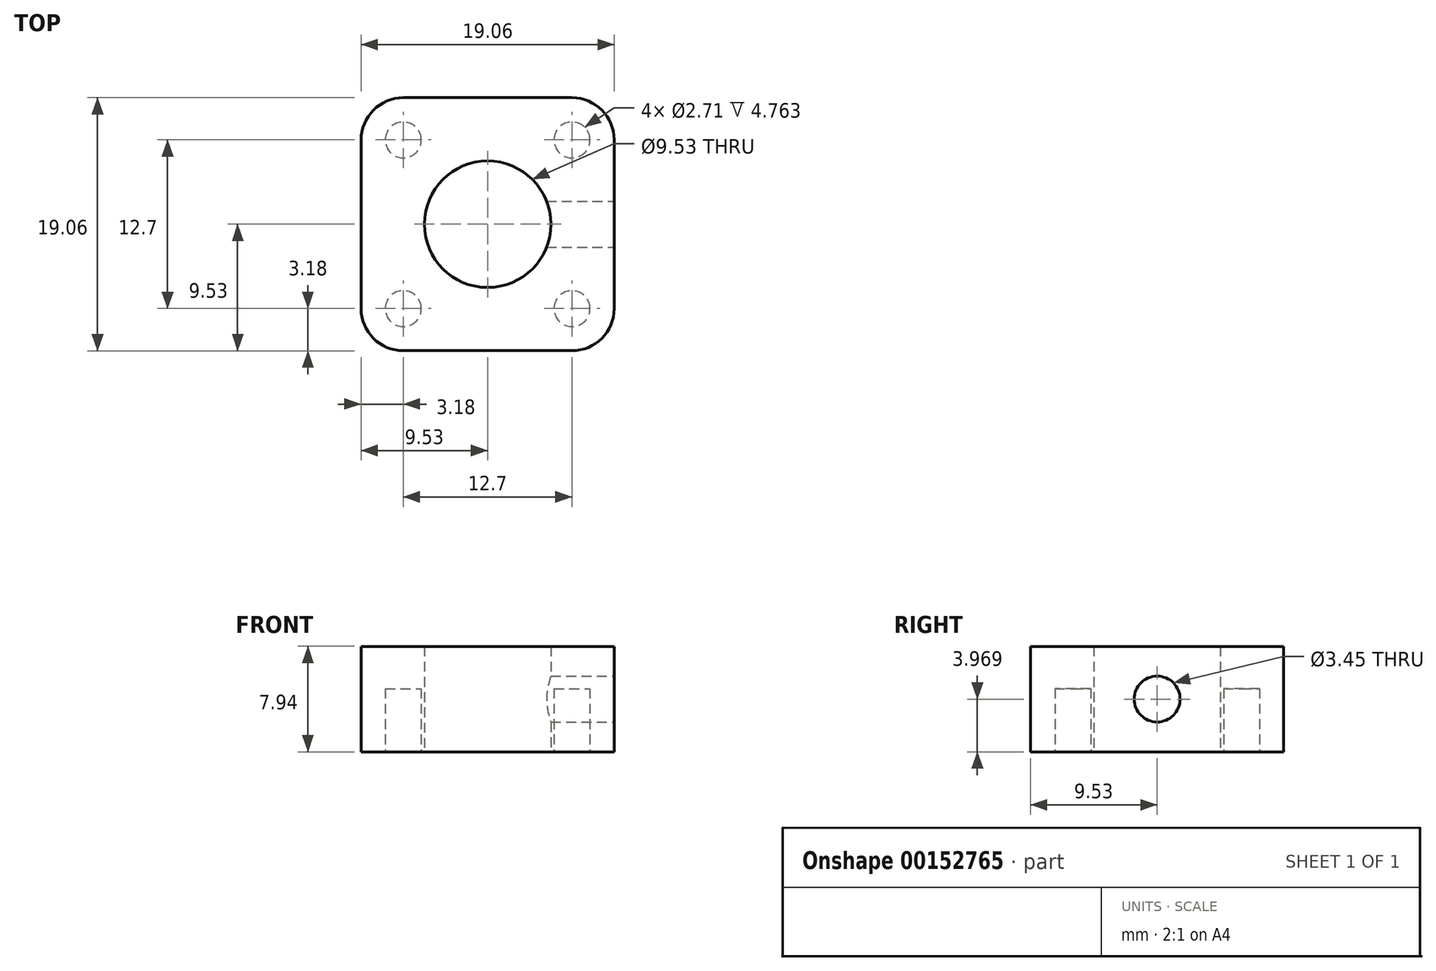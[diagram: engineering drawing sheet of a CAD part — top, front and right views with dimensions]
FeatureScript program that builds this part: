
annotation { "Feature Type Name" : "Feature", "Feature Type Description" : "" }
export const myFeature = defineFeature(function(context is Context, id is Id, definition is map)
    precondition{}
    {
        {
            var Q0;
            Q0=qCreatedBy(makeId("Top.planeOp"),FACE);
            var sketch = newSketch(context, id + "F0", { "sketchPlane" : qUnion([Q0])});
            skLineSegment(sketch, "E0", {"start": v(0, 0) * mm, "end": v(0, -9.52) * mm, "construction": true});
            skLineSegment(sketch, "E1.bottom", {"start": v(9.52, -9.52) * mm, "end": v(-9.52, -9.52) * mm});
            skLineSegment(sketch, "E1.top", {"start": v(9.52, 9.52) * mm, "end": v(-9.52, 9.52) * mm});
            skLineSegment(sketch, "E1.left", {"start": v(9.52, -9.53) * mm, "end": v(9.52, 9.52) * mm});
            skLineSegment(sketch, "E1.right", {"start": v(-9.52, -9.52) * mm, "end": v(-9.52, 9.52) * mm});
            skLineSegment(sketch, "E2.bottom", {"start": v(-6.35, 6.35) * mm, "end": v(6.35, 6.35) * mm, "construction": true});
            skLineSegment(sketch, "E2.top", {"start": v(-6.35, -6.35) * mm, "end": v(6.35, -6.35) * mm, "construction": true});
            skLineSegment(sketch, "E2.left", {"start": v(-6.35, 6.35) * mm, "end": v(-6.35, -6.35) * mm, "construction": true});
            skLineSegment(sketch, "E2.right", {"start": v(6.35, 6.35) * mm, "end": v(6.35, -6.35) * mm, "construction": true});
            skPoint(sketch, "E2.middle", {"position": v(0, 0) * mm});
            skCircle(sketch, "E3", {"center": v(-6.35, 6.35) * mm, "radius": 3.18 * mm, "construction": true});
            skLineSegment(sketch, "E4", {"start": v(0, 0) * mm, "end": v(0, 9.52) * mm, "construction": true});
            skCircle(sketch, "E5", {"center": v(-6.35, 6.35) * mm, "radius": 1.83 * mm, "construction": true});
            skCircle(sketch, "E6", {"center": v(6.35, 6.35) * mm, "radius": 1.83 * mm, "construction": true});
            skCircle(sketch, "E7", {"center": v(6.35, -6.35) * mm, "radius": 1.83 * mm, "construction": true});
            skCircle(sketch, "E8", {"center": v(-6.35, -6.35) * mm, "radius": 1.83 * mm, "construction": true});
            skCircle(sketch, "E9", {"center": v(0, 0) * mm, "radius": 4.76 * mm});
            skSolve(sketch);
        }
        {
            var Q0;
            Q0=qSketchRegion(id+"F0",true);
            extrude(context, id + "F1", {"entities" : qUnion([Q0]), "depth" : 7.94 * mm});
        }
        {
            var Q0;
            Q0=makeQuery(id+"F1.opExtrude","SWEPT_EDGE",EDGE,{"disambiguationData":[OSD([sQuery(id+"F0.wireOp",EDGE,"E1.top"),sQuery(id+"F0.wireOp",EDGE,"E1.right")])]});
            var Q1;
            Q1=makeQuery(id+"F1.opExtrude","SWEPT_EDGE",EDGE,{"disambiguationData":[OSD([sQuery(id+"F0.wireOp",EDGE,"E1.bottom"),sQuery(id+"F0.wireOp",EDGE,"E1.right")])]});
            var Q2;
            Q2=makeQuery(id+"F1.opExtrude","SWEPT_EDGE",EDGE,{"disambiguationData":[OSD([sQuery(id+"F0.wireOp",EDGE,"E1.bottom"),sQuery(id+"F0.wireOp",EDGE,"E1.left")])]});
            var Q3;
            Q3=makeQuery(id+"F1.opExtrude","SWEPT_EDGE",EDGE,{"disambiguationData":[OSD([sQuery(id+"F0.wireOp",EDGE,"E1.top"),sQuery(id+"F0.wireOp",EDGE,"E1.left")])]});
            fillet(context, id + "F2", {"entities" : qUnion([Q0, Q1, Q2, Q3]), "radius" : 3.17 * mm, "tangentPropagation" : true, "allowEdgeOverflow" : false});
        }
        {
            var Q0;
            Q0=makeQuery(id+"F1.opExtrude","CAP_FACE",FACE,{"disambiguationData":[OSD([sQuery(id+"F0.wireOp",EDGE,"E1.bottom"),sQuery(id+"F0.wireOp",EDGE,"E1.top"),sQuery(id+"F0.wireOp",EDGE,"E1.left"),sQuery(id+"F0.wireOp",EDGE,"E1.right"),sQuery(id+"F0.wireOp",EDGE,"E9")])],"isStart":true});
            var sketch = newSketch(context, id + "F3", { "sketchPlane" : qUnion([Q0])});
            skCircle(sketch, "E10", {"center": v(6.35, 6.35) * mm, "radius": 1.35 * mm});
            skCircle(sketch, "E11", {"center": v(-6.35, 6.35) * mm, "radius": 1.35 * mm});
            skCircle(sketch, "E12", {"center": v(-6.35, -6.35) * mm, "radius": 1.35 * mm});
            skCircle(sketch, "E13", {"center": v(6.35, -6.35) * mm, "radius": 1.35 * mm});
            skSolve(sketch);
        }
        {
            var Q0;
            Q0=qSketchRegion(id+"F3",true);
            extrude(context, id + "F4", {"entities" : qUnion([Q0]), "operationType" : NewBodyOperationType.REMOVE, "oppositeDirection" : true, "depth" : 4.76 * mm});
        }
        {
            var Q0;
            Q0=makeQuery(id+"F1.opExtrude","SWEPT_FACE",FACE,{"disambiguationData":[OSD([sQuery(id+"F0.wireOp",EDGE,"E1.left")])]});
            var sketch = newSketch(context, id + "F5", { "sketchPlane" : qUnion([Q0])});
            skLineSegment(sketch, "E14", {"start": v(0, 7.94) * mm, "end": v(0, 0) * mm, "construction": true});
            skCircle(sketch, "E15", {"center": v(0, 3.97) * mm, "radius": 1.73 * mm});
            skSolve(sketch);
        }
        {
            var Q0;
            Q0 = qSketchRegion(id + "F5", true);
            var Q1;
            Q1=makeQuery(id+"F1.opExtrude","SWEPT_FACE",FACE,{"disambiguationData":[OSD([sQuery(id+"F0.wireOp",EDGE,"E9")])]});
            extrude(context, id + "F6", {"entities" : qUnion([Q0]), "operationType" : NewBodyOperationType.REMOVE, "endBound" : BoundingType.UP_TO_SURFACE, "oppositeDirection" : true, "endBoundEntityFace" : qUnion([Q1]), "depth" : 25.4 * mm});
        }
    });
